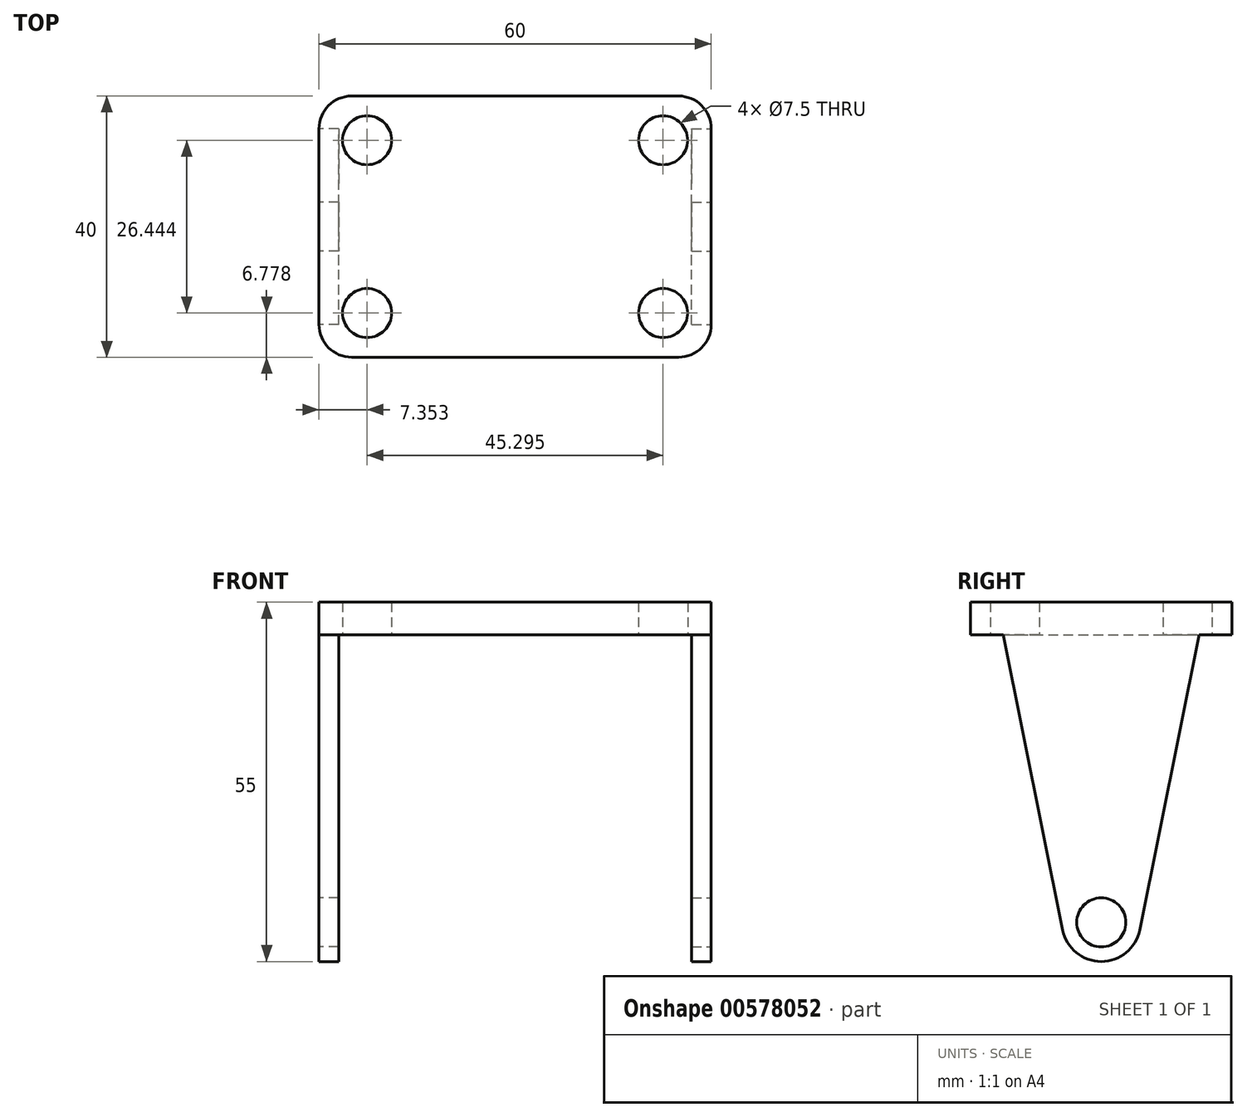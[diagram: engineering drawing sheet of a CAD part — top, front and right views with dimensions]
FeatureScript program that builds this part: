
annotation { "Feature Type Name" : "Feature", "Feature Type Description" : "" }
export const myFeature = defineFeature(function(context is Context, id is Id, definition is map)
    precondition{}
    {
        {
            var Q0;
            Q0=qCreatedBy(makeId("Top.planeOp"),FACE);
            var sketch = newSketch(context, id + "F0", { "sketchPlane" : qUnion([Q0])});
            skLineSegment(sketch, "E0.bottom", {"start": v(30, -20) * mm, "end": v(-30, -20) * mm});
            skLineSegment(sketch, "E0.top", {"start": v(30, 20) * mm, "end": v(-30, 20) * mm});
            skLineSegment(sketch, "E0.left", {"start": v(30, -20) * mm, "end": v(30, 20) * mm});
            skLineSegment(sketch, "E0.right", {"start": v(-30, -20) * mm, "end": v(-30, 20) * mm});
            skPoint(sketch, "E0.middle", {"position": v(0, 0) * mm});
            skCircle(sketch, "E1", {"center": v(-22.65, 13.22) * mm, "radius": 3.75 * mm});
            skCircle(sketch, "E2", {"center": v(-22.65, -13.22) * mm, "radius": 3.75 * mm});
            skCircle(sketch, "E3.MirrorC", {"center": v(22.65, 13.22) * mm, "radius": 3.75 * mm});
            skCircle(sketch, "E4.MirrorC", {"center": v(22.65, -13.22) * mm, "radius": 3.75 * mm});
            skSolve(sketch);
        }
        {
            var Q0;
            Q0 = qSketchRegion(id + "F0", true);
            extrude(context, id + "F1", {"entities" : qUnion([Q0]), "depth" : 5 * mm, "offsetDistance" : 25 * mm});
        }
        {
            var Q0;
            Q0=makeQuery(id+"F1.opExtrude","SWEPT_EDGE",EDGE,{"disambiguationData":[OSD([sQuery(id+"F0.wireOp",EDGE,"E0.bottom"),sQuery(id+"F0.wireOp",EDGE,"E0.right")])]});
            var Q1;
            Q1=makeQuery(id+"F1.opExtrude","SWEPT_EDGE",EDGE,{"disambiguationData":[OSD([sQuery(id+"F0.wireOp",EDGE,"E0.bottom"),sQuery(id+"F0.wireOp",EDGE,"E0.left")])]});
            var Q2;
            Q2=makeQuery(id+"F1.opExtrude","SWEPT_EDGE",EDGE,{"disambiguationData":[OSD([sQuery(id+"F0.wireOp",EDGE,"E0.top"),sQuery(id+"F0.wireOp",EDGE,"E0.left")])]});
            var Q3;
            Q3=makeQuery(id+"F1.opExtrude","SWEPT_EDGE",EDGE,{"disambiguationData":[OSD([sQuery(id+"F0.wireOp",EDGE,"E0.top"),sQuery(id+"F0.wireOp",EDGE,"E0.right")])]});
            fillet(context, id + "F2", {"entities" : qUnion([Q0, Q1, Q2, Q3]), "radius" : 5 * mm, "tangentPropagation" : true, "allowEdgeOverflow" : false});
        }
        {
            var Q0;
            Q0=makeQuery(id+"F1.opExtrude","SWEPT_FACE",FACE,{"disambiguationData":[OSD([sQuery(id+"F0.wireOp",EDGE,"E0.left")])]});
            var sketch = newSketch(context, id + "F3", { "sketchPlane" : qUnion([Q0])});
            skLineSegment(sketch, "E5", {"start": v(-15, 0) * mm, "end": v(-5.88, -45.19) * mm});
            skLineSegment(sketch, "E6", {"start": v(15, 0) * mm, "end": v(5.88, -45.19) * mm});
            skArc(sketch, "E7", {"start": v(-5.88, -45.19) * mm, "mid": v(0, -50) * mm, "end": v(5.88, -45.19) * mm});
            skCircle(sketch, "E8", {"center": v(0, -44) * mm, "radius": 3.75 * mm});
            skSolve(sketch);
        }
        {
            var Q0;
            Q0=makeQuery(id+"F3.imprint","IMPRINT",FACE,{"disambiguationData":[TD([[makeQuery(id+"F3.imprint","IMPRINT",EDGE,{"derivedFrom":sQuery(id+"F3.wireOp",EDGE,"E5")}),1.0]])]});
            extrude(context, id + "F4", {"entities" : qUnion([Q0]), "operationType" : NewBodyOperationType.ADD, "oppositeDirection" : true, "depth" : 3 * mm, "offsetDistance" : 25 * mm});
        }
        {
            var Q0;
            Q0=makeQuery(id+"F1.opExtrude","SWEPT_BODY",BODY,{"disambiguationData":[OSD([sQuery(id+"F0.wireOp",EDGE,"E0.bottom"),sQuery(id+"F0.wireOp",EDGE,"E0.top"),sQuery(id+"F0.wireOp",EDGE,"E0.left"),sQuery(id+"F0.wireOp",EDGE,"E0.right"),sQuery(id+"F0.wireOp",EDGE,"E1"),sQuery(id+"F0.wireOp",EDGE,"E2"),sQuery(id+"F0.wireOp",EDGE,"E3.MirrorC"),sQuery(id+"F0.wireOp",EDGE,"E4.MirrorC")])]});
            var Q1;
            Q1=qCreatedBy(makeId("Right.planeOp"),FACE);
            mirror(context, id + "F5", {"operationType" : NewBodyOperationType.ADD, "entities" : qUnion([Q0]), "mirrorPlane" : qUnion([Q1])});
        }
    });
